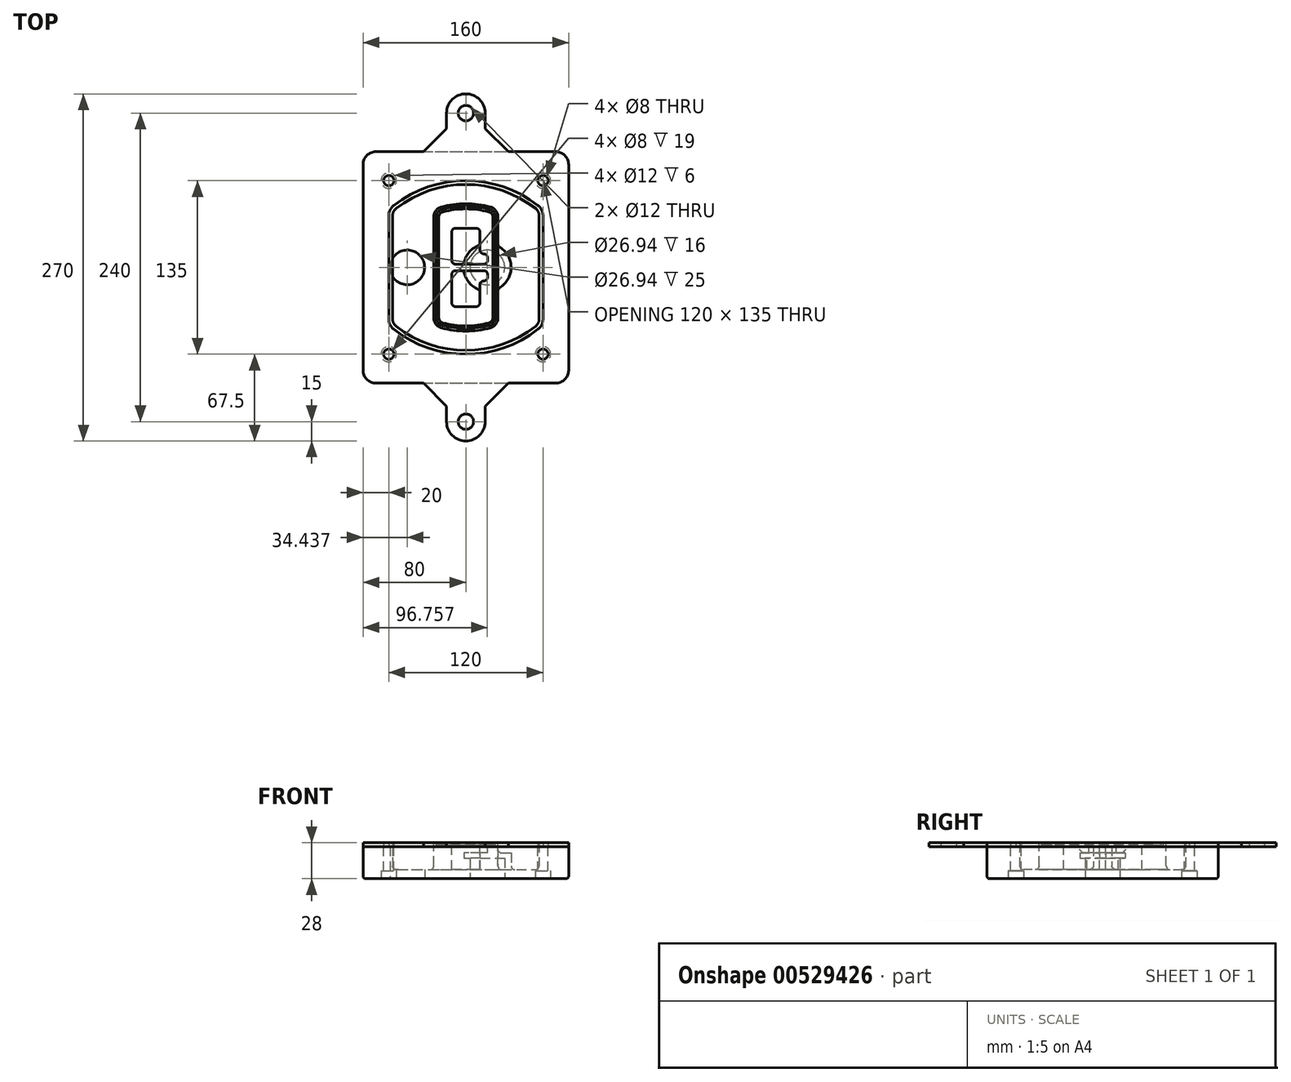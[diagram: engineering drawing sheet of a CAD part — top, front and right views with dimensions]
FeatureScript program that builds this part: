
annotation { "Feature Type Name" : "Feature", "Feature Type Description" : "" }
export const myFeature = defineFeature(function(context is Context, id is Id, definition is map)
    precondition{}
    {
        {
            var Q0;
            Q0=qCreatedBy(makeId("Top.planeOp"),FACE);
            var sketch = newSketch(context, id + "F0", { "sketchPlane" : qUnion([Q0])});
            skPoint(sketch, "E0.rect.middle", {"position": v(0, 0) * mm});
            skLineSegment(sketch, "E1.bottom", {"start": v(-70, -90) * mm, "end": v(70, -90) * mm});
            skLineSegment(sketch, "E1.top", {"start": v(-70, 90) * mm, "end": v(70, 90) * mm});
            skLineSegment(sketch, "E1.left", {"start": v(-80, -80) * mm, "end": v(-80, 80) * mm});
            skLineSegment(sketch, "E1.right", {"start": v(80, -80) * mm, "end": v(80, 80) * mm});
            skLineSegment(sketch, "E2", {"start": v(-80, 90) * mm, "end": v(80, -90) * mm, "construction": true});
            skLineSegment(sketch, "E3", {"start": v(80, 90) * mm, "end": v(-80, -90) * mm, "construction": true});
            skCircle(sketch, "E4", {"center": v(-60, 67.5) * mm, "radius": 4 * mm});
            skCircle(sketch, "E5", {"center": v(60, 67.5) * mm, "radius": 4 * mm});
            skCircle(sketch, "E6", {"center": v(60, -67.5) * mm, "radius": 4 * mm});
            skCircle(sketch, "E7", {"center": v(-60, -67.5) * mm, "radius": 4 * mm});
            skLineSegment(sketch, "E8", {"start": v(-60, 67.5) * mm, "end": v(60, 67.5) * mm, "construction": true});
            skLineSegment(sketch, "E9", {"start": v(60, 67.5) * mm, "end": v(60, -67.5) * mm, "construction": true});
            skLineSegment(sketch, "E10", {"start": v(60, -67.5) * mm, "end": v(-60, -67.5) * mm, "construction": true});
            skLineSegment(sketch, "E11", {"start": v(-60, -67.5) * mm, "end": v(-60, 67.5) * mm, "construction": true});
            skLineSegment(sketch, "E12", {"start": v(-60, 40.3) * mm, "end": v(-60, -40.3) * mm});
            skLineSegment(sketch, "E13", {"start": v(60, 40.3) * mm, "end": v(60, -40.3) * mm});
            skArc(sketch, "E14", {"start": v(56.15, 48.18) * mm, "mid": v(0, 67.5) * mm, "end": v(-56.15, 48.18) * mm});
            skArc(sketch, "E15", {"start": v(-56.15, -48.18) * mm, "mid": v(0, -67.5) * mm, "end": v(56.15, -48.18) * mm});
            skLineSegment(sketch, "E16", {"start": v(-60, 0) * mm, "end": v(60, 0) * mm, "construction": true});
            skPoint(sketch, "E17.visualSharp", {"position": v(-60, -45) * mm});
            skArc(sketch, "E17.filletArc", {"start": v(-60, -40.3) * mm, "mid": v(-58.99, -44.68) * mm, "end": v(-56.15, -48.18) * mm});
            skPoint(sketch, "E18.visualSharp", {"position": v(-60, 45) * mm});
            skArc(sketch, "E18.filletArc", {"start": v(-56.15, 48.18) * mm, "mid": v(-58.99, 44.68) * mm, "end": v(-60, 40.3) * mm});
            skPoint(sketch, "E19.visualSharp", {"position": v(60, 45) * mm});
            skArc(sketch, "E19.filletArc", {"start": v(60, 40.3) * mm, "mid": v(58.99, 44.68) * mm, "end": v(56.15, 48.18) * mm});
            skPoint(sketch, "E20.visualSharp", {"position": v(60, -45) * mm});
            skArc(sketch, "E20.filletArc", {"start": v(56.15, -48.18) * mm, "mid": v(58.99, -44.68) * mm, "end": v(60, -40.3) * mm});
            skPoint(sketch, "E21.visualSharp", {"position": v(-80, 90) * mm});
            skArc(sketch, "E21.filletArc", {"start": v(-70, 90) * mm, "mid": v(-77.07, 87.07) * mm, "end": v(-80, 80) * mm});
            skPoint(sketch, "E22.visualSharp", {"position": v(80, 90) * mm});
            skArc(sketch, "E22.filletArc", {"start": v(80, 80) * mm, "mid": v(77.07, 87.07) * mm, "end": v(70, 90) * mm});
            skPoint(sketch, "E23.visualSharp", {"position": v(80, -90) * mm});
            skArc(sketch, "E23.filletArc", {"start": v(70, -90) * mm, "mid": v(77.07, -87.07) * mm, "end": v(80, -80) * mm});
            skPoint(sketch, "E24.visualSharp", {"position": v(-80, -90) * mm});
            skArc(sketch, "E24.filletArc", {"start": v(-80, -80) * mm, "mid": v(-77.07, -87.07) * mm, "end": v(-70, -90) * mm});
            skArc(sketch, "E25.0", {"start": v(57, 40.3) * mm, "mid": v(56.3, 43.36) * mm, "end": v(54.3, 45.81) * mm});
            skLineSegment(sketch, "E25.1", {"start": v(57, 40.3) * mm, "end": v(57, -40.3) * mm});
            skArc(sketch, "E25.2", {"start": v(54.3, -45.81) * mm, "mid": v(56.3, -43.36) * mm, "end": v(57, -40.3) * mm});
            skArc(sketch, "E25.3", {"start": v(-54.3, -45.81) * mm, "mid": v(0, -64.5) * mm, "end": v(54.3, -45.81) * mm});
            skArc(sketch, "E25.4", {"start": v(-57, -40.3) * mm, "mid": v(-56.3, -43.36) * mm, "end": v(-54.3, -45.81) * mm});
            skArc(sketch, "E25.5", {"start": v(54.3, 45.81) * mm, "mid": v(0, 64.5) * mm, "end": v(-54.3, 45.81) * mm});
            skLineSegment(sketch, "E25.6", {"start": v(-57, 40.3) * mm, "end": v(-57, -40.3) * mm});
            skArc(sketch, "E25.7", {"start": v(-54.3, 45.81) * mm, "mid": v(-56.3, 43.36) * mm, "end": v(-57, 40.3) * mm});
            skArc(sketch, "E26.0", {"start": v(-58.62, 51.33) * mm, "mid": v(-62.58, 46.43) * mm, "end": v(-64, 40.3) * mm});
            skArc(sketch, "E26.1", {"start": v(58.62, 51.33) * mm, "mid": v(0, 71.5) * mm, "end": v(-58.62, 51.33) * mm});
            skArc(sketch, "E26.2", {"start": v(64, 40.3) * mm, "mid": v(62.58, 46.43) * mm, "end": v(58.62, 51.33) * mm});
            skLineSegment(sketch, "E26.3", {"start": v(64, 40.3) * mm, "end": v(64, -40.3) * mm});
            skArc(sketch, "E26.4", {"start": v(58.62, -51.33) * mm, "mid": v(62.58, -46.43) * mm, "end": v(64, -40.3) * mm});
            skLineSegment(sketch, "E26.5", {"start": v(-64, 40.3) * mm, "end": v(-64, -40.3) * mm});
            skArc(sketch, "E26.6", {"start": v(-58.62, -51.33) * mm, "mid": v(0, -71.5) * mm, "end": v(58.62, -51.33) * mm});
            skArc(sketch, "E26.7", {"start": v(-64, -40.3) * mm, "mid": v(-62.58, -46.43) * mm, "end": v(-58.62, -51.33) * mm});
            skSolve(sketch);
        }
        {
            var Q0;
            Q0=makeQuery(id+"F0.imprint","IMPRINT",FACE,{"disambiguationData":[TD([[makeQuery(id+"F0.imprint","IMPRINT",EDGE,{"derivedFrom":sQuery(id+"F0.wireOp",EDGE,"E1.bottom")}),1.0]])]});
            var Q1;
            Q1=makeQuery(id+"F0.imprint","IMPRINT",FACE,{"disambiguationData":[TD([[makeQuery(id+"F0.imprint","IMPRINT",EDGE,{"derivedFrom":sQuery(id+"F0.wireOp",EDGE,"E12")}),1.0]])]});
            var Q2;
            Q2=makeQuery(id+"F0.imprint","IMPRINT",FACE,{"disambiguationData":[TD([[makeQuery(id+"F0.imprint","IMPRINT",EDGE,{"derivedFrom":sQuery(id+"F0.wireOp",EDGE,"E25.0")}),1.0]])]});
            var Q3;
            Q3=makeQuery(id+"F0.imprint","IMPRINT",FACE,{"disambiguationData":[TD([[makeQuery(id+"F0.imprint","IMPRINT",EDGE,{"derivedFrom":sQuery(id+"F0.wireOp",EDGE,"E12")}),-1.0]])]});
            extrude(context, id + "F1", {"entities" : qUnion([Q0, Q1, Q2, Q3]), "oppositeDirection" : true, "depth" : 25 * mm});
        }
        {
            var Q0;
            Q0=makeQuery(id+"F0.imprint","IMPRINT",FACE,{"disambiguationData":[TD([[makeQuery(id+"F0.imprint","IMPRINT",EDGE,{"derivedFrom":sQuery(id+"F0.wireOp",EDGE,"E12")}),1.0]])]});
            extrude(context, id + "F2", {"entities" : qUnion([Q0]), "operationType" : NewBodyOperationType.ADD, "depth" : 3 * mm});
        }
        {
            var Q0;
            Q0=makeQuery(id+"F0.imprint","IMPRINT",FACE,{"disambiguationData":[TD([[makeQuery(id+"F0.imprint","IMPRINT",EDGE,{"derivedFrom":sQuery(id+"F0.wireOp",EDGE,"E25.0")}),1.0]])]});
            extrude(context, id + "F3", {"entities" : qUnion([Q0]), "operationType" : NewBodyOperationType.REMOVE, "oppositeDirection" : true, "depth" : 18 * mm});
        }
        {
            var Q0;
            Q0=makeQuery(id+"F2.opExtrude","CAP_FACE",FACE,{"disambiguationData":[OSD([sQuery(id+"F0.wireOp",EDGE,"E12"),sQuery(id+"F0.wireOp",EDGE,"E13"),sQuery(id+"F0.wireOp",EDGE,"E14"),sQuery(id+"F0.wireOp",EDGE,"E15"),sQuery(id+"F0.wireOp",EDGE,"E17.filletArc"),sQuery(id+"F0.wireOp",EDGE,"E18.filletArc"),sQuery(id+"F0.wireOp",EDGE,"E19.filletArc"),sQuery(id+"F0.wireOp",EDGE,"E20.filletArc"),sQuery(id+"F0.wireOp",EDGE,"E25.0"),sQuery(id+"F0.wireOp",EDGE,"E25.1"),sQuery(id+"F0.wireOp",EDGE,"E25.2"),sQuery(id+"F0.wireOp",EDGE,"E25.3"),sQuery(id+"F0.wireOp",EDGE,"E25.4"),sQuery(id+"F0.wireOp",EDGE,"E25.5"),sQuery(id+"F0.wireOp",EDGE,"E25.6"),sQuery(id+"F0.wireOp",EDGE,"E25.7")])],"isStart":false});
            var sketch = newSketch(context, id + "F4", { "sketchPlane" : qUnion([Q0])});
            skArc(sketch, "E27.0", {"start": v(-19.08, -46.97) * mm, "mid": v(0, -49.5) * mm, "end": v(19.08, -46.97) * mm});
            skArc(sketch, "E28.0", {"start": v(19.08, 46.97) * mm, "mid": v(0, 49.5) * mm, "end": v(-19.08, 46.97) * mm});
            skLineSegment(sketch, "E29", {"start": v(-25, 39.25) * mm, "end": v(-25, -39.25) * mm});
            skLineSegment(sketch, "E30", {"start": v(25, 39.25) * mm, "end": v(25, -39.25) * mm});
            skLineSegment(sketch, "E31", {"start": v(-25, 45.1) * mm, "end": v(25, 45.1) * mm, "construction": true});
            skLineSegment(sketch, "E32", {"start": v(-25, -45.1) * mm, "end": v(25, -45.1) * mm, "construction": true});
            skPoint(sketch, "E33.visualSharp", {"position": v(-25, 45.1) * mm});
            skArc(sketch, "E33.filletArc", {"start": v(-19.08, 46.97) * mm, "mid": v(-23.35, 44.11) * mm, "end": v(-25, 39.25) * mm});
            skPoint(sketch, "E34.visualSharp", {"position": v(25, 45.1) * mm});
            skArc(sketch, "E34.filletArc", {"start": v(25, 39.25) * mm, "mid": v(23.35, 44.11) * mm, "end": v(19.08, 46.97) * mm});
            skPoint(sketch, "E35.visualSharp", {"position": v(25, -45.1) * mm});
            skArc(sketch, "E35.filletArc", {"start": v(19.08, -46.97) * mm, "mid": v(23.35, -44.11) * mm, "end": v(25, -39.25) * mm});
            skPoint(sketch, "E36.visualSharp", {"position": v(-25, -45.1) * mm});
            skArc(sketch, "E36.filletArc", {"start": v(-25, -39.25) * mm, "mid": v(-23.35, -44.11) * mm, "end": v(-19.08, -46.97) * mm});
            skArc(sketch, "E37.0", {"start": v(54.3, 45.81) * mm, "mid": v(0, 64.5) * mm, "end": v(-54.3, 45.81) * mm});
            skArc(sketch, "E37.1", {"start": v(-54.3, 45.81) * mm, "mid": v(-56.3, 43.36) * mm, "end": v(-57, 40.3) * mm});
            skLineSegment(sketch, "E37.2", {"start": v(-57, 40.3) * mm, "end": v(-57, -40.3) * mm});
            skArc(sketch, "E37.3", {"start": v(-57, -40.3) * mm, "mid": v(-56.3, -43.36) * mm, "end": v(-54.3, -45.81) * mm});
            skArc(sketch, "E37.4", {"start": v(-54.3, -45.81) * mm, "mid": v(0, -64.5) * mm, "end": v(54.3, -45.81) * mm});
            skArc(sketch, "E37.5", {"start": v(54.3, -45.81) * mm, "mid": v(56.3, -43.36) * mm, "end": v(57, -40.3) * mm});
            skLineSegment(sketch, "E37.6", {"start": v(57, 40.3) * mm, "end": v(57, -40.3) * mm});
            skArc(sketch, "E37.7", {"start": v(57, 40.3) * mm, "mid": v(56.3, 43.36) * mm, "end": v(54.3, 45.81) * mm});
            skLineSegment(sketch, "E38.0", {"start": v(23, 39.25) * mm, "end": v(23, -39.25) * mm});
            skArc(sketch, "E38.1", {"start": v(18.56, -45.04) * mm, "mid": v(21.76, -42.9) * mm, "end": v(23, -39.25) * mm});
            skArc(sketch, "E38.2", {"start": v(-18.56, -45.04) * mm, "mid": v(0, -47.5) * mm, "end": v(18.56, -45.04) * mm});
            skArc(sketch, "E38.3", {"start": v(-23, -39.25) * mm, "mid": v(-21.76, -42.9) * mm, "end": v(-18.56, -45.04) * mm});
            skLineSegment(sketch, "E38.4", {"start": v(-23, 39.25) * mm, "end": v(-23, -39.25) * mm});
            skArc(sketch, "E38.5", {"start": v(23, 39.25) * mm, "mid": v(21.76, 42.9) * mm, "end": v(18.56, 45.04) * mm});
            skArc(sketch, "E38.6", {"start": v(-18.56, 45.04) * mm, "mid": v(-21.76, 42.9) * mm, "end": v(-23, 39.25) * mm});
            skArc(sketch, "E38.7", {"start": v(18.56, 45.04) * mm, "mid": v(0, 47.5) * mm, "end": v(-18.56, 45.04) * mm});
            skArc(sketch, "E39.0", {"start": v(21, 39.25) * mm, "mid": v(20.18, 41.68) * mm, "end": v(18.04, 43.1) * mm});
            skLineSegment(sketch, "E39.1", {"start": v(21, 39.25) * mm, "end": v(21, -39.25) * mm});
            skArc(sketch, "E39.2", {"start": v(18.04, -43.1) * mm, "mid": v(20.18, -41.68) * mm, "end": v(21, -39.25) * mm});
            skArc(sketch, "E39.3", {"start": v(-18.04, -43.1) * mm, "mid": v(0, -45.5) * mm, "end": v(18.04, -43.1) * mm});
            skArc(sketch, "E39.4", {"start": v(-21, -39.25) * mm, "mid": v(-20.18, -41.68) * mm, "end": v(-18.04, -43.1) * mm});
            skArc(sketch, "E39.5", {"start": v(18.04, 43.1) * mm, "mid": v(0, 45.5) * mm, "end": v(-18.04, 43.1) * mm});
            skLineSegment(sketch, "E39.6", {"start": v(-21, 39.25) * mm, "end": v(-21, -39.25) * mm});
            skArc(sketch, "E39.7", {"start": v(-18.04, 43.1) * mm, "mid": v(-20.18, 41.68) * mm, "end": v(-21, 39.25) * mm});
            skLineSegment(sketch, "E40", {"start": v(-25, 0) * mm, "end": v(25, 0) * mm, "construction": true});
            skLineSegment(sketch, "E41", {"start": v(-11, 5.5) * mm, "end": v(-11, 27.5) * mm});
            skLineSegment(sketch, "E42", {"start": v(-8, 30.5) * mm, "end": v(8, 30.5) * mm});
            skLineSegment(sketch, "E43", {"start": v(11, 27.5) * mm, "end": v(11, 13.5) * mm});
            skLineSegment(sketch, "E44", {"start": v(14, 10.5) * mm, "end": v(14, 10.5) * mm});
            skLineSegment(sketch, "E45", {"start": v(17, 7.5) * mm, "end": v(17, 5.5) * mm});
            skLineSegment(sketch, "E46", {"start": v(14, 2.5) * mm, "end": v(-8, 2.5) * mm});
            skPoint(sketch, "E47.visualSharp", {"position": v(-11, 30.5) * mm});
            skArc(sketch, "E47.filletArc", {"start": v(-8, 30.5) * mm, "mid": v(-10.12, 29.62) * mm, "end": v(-11, 27.5) * mm});
            skPoint(sketch, "E48.visualSharp", {"position": v(11, 30.5) * mm});
            skArc(sketch, "E48.filletArc", {"start": v(11, 27.5) * mm, "mid": v(10.12, 29.62) * mm, "end": v(8, 30.5) * mm});
            skPoint(sketch, "E49.visualSharp", {"position": v(11, 10.5) * mm});
            skArc(sketch, "E49.filletArc", {"start": v(11, 13.5) * mm, "mid": v(11.88, 11.38) * mm, "end": v(14, 10.5) * mm});
            skPoint(sketch, "E50.visualSharp", {"position": v(17, 10.5) * mm});
            skArc(sketch, "E50.filletArc", {"start": v(17, 7.5) * mm, "mid": v(16.12, 9.62) * mm, "end": v(14, 10.5) * mm});
            skPoint(sketch, "E51.visualSharp", {"position": v(17, 2.5) * mm});
            skArc(sketch, "E51.filletArc", {"start": v(14, 2.5) * mm, "mid": v(16.12, 3.38) * mm, "end": v(17, 5.5) * mm});
            skPoint(sketch, "E52.visualSharp", {"position": v(-11, 2.5) * mm});
            skArc(sketch, "E52.filletArc", {"start": v(-11, 5.5) * mm, "mid": v(-10.12, 3.38) * mm, "end": v(-8, 2.5) * mm});
            skLineSegment(sketch, "E53.0.MirrorCS", {"start": v(14, -2.5) * mm, "end": v(-8, -2.5) * mm});
            skArc(sketch, "E54.0.MirrorCS", {"start": v(-11, -5.5) * mm, "mid": v(-10.12, -3.38) * mm, "end": v(-8, -2.5) * mm});
            skLineSegment(sketch, "E55.0.MirrorCS", {"start": v(-11, -5.5) * mm, "end": v(-11, -27.5) * mm});
            skArc(sketch, "E56.0.MirrorCS", {"start": v(-8, -30.5) * mm, "mid": v(-10.12, -29.62) * mm, "end": v(-11, -27.5) * mm});
            skLineSegment(sketch, "E57.0.MirrorCS", {"start": v(-8, -30.5) * mm, "end": v(8, -30.5) * mm});
            skArc(sketch, "E58.0.MirrorCS", {"start": v(11, -27.5) * mm, "mid": v(10.12, -29.62) * mm, "end": v(8, -30.5) * mm});
            skLineSegment(sketch, "E59.0.MirrorCS", {"start": v(11, -27.5) * mm, "end": v(11, -13.5) * mm});
            skArc(sketch, "E60.0.MirrorCS", {"start": v(11, -13.5) * mm, "mid": v(11.88, -11.38) * mm, "end": v(14, -10.5) * mm});
            skArc(sketch, "E61.0.MirrorCS", {"start": v(17, -7.5) * mm, "mid": v(16.12, -9.62) * mm, "end": v(14, -10.5) * mm});
            skLineSegment(sketch, "E62.0.MirrorCS", {"start": v(17, -7.5) * mm, "end": v(17, -5.5) * mm});
            skArc(sketch, "E63.0.MirrorCS", {"start": v(14, -2.5) * mm, "mid": v(16.12, -3.38) * mm, "end": v(17, -5.5) * mm});
            skSolve(sketch);
        }
        {
            var Q0;
            Q0=makeQuery(id+"F4.imprint","IMPRINT",FACE,{"disambiguationData":[TD([[makeQuery(id+"F4.imprint","IMPRINT",EDGE,{"derivedFrom":sQuery(id+"F4.wireOp",EDGE,"E27.0")}),1.0]])]});
            var Q1;
            Q1=makeQuery(id+"F4.imprint","IMPRINT",FACE,{"disambiguationData":[TD([[makeQuery(id+"F4.imprint","IMPRINT",EDGE,{"derivedFrom":sQuery(id+"F4.wireOp",EDGE,"E38.0")}),-1.0]])]});
            var Q2;
            Q2=makeQuery(id+"F4.imprint","IMPRINT",FACE,{"disambiguationData":[TD([[makeQuery(id+"F4.imprint","IMPRINT",EDGE,{"derivedFrom":sQuery(id+"F4.wireOp",EDGE,"E39.0")}),1.0]])]});
            extrude(context, id + "F5", {"entities" : qUnion([Q0, Q1, Q2]), "operationType" : NewBodyOperationType.ADD, "endBound" : BoundingType.UP_TO_NEXT, "oppositeDirection" : true, "depth" : 25 * mm});
        }
        {
            var Q0;
            Q0=makeQuery(id+"F4.imprint","IMPRINT",FACE,{"disambiguationData":[TD([[makeQuery(id+"F4.imprint","IMPRINT",EDGE,{"derivedFrom":sQuery(id+"F4.wireOp",EDGE,"E38.0")}),-1.0]])]});
            extrude(context, id + "F6", {"entities" : qUnion([Q0]), "operationType" : NewBodyOperationType.REMOVE, "oppositeDirection" : true, "depth" : 2 * mm, "offsetDistance" : 25 * mm});
        }
        {
            var Q0;
            Q0=makeQuery(id+"F1.opExtrude","CAP_FACE",FACE,{"disambiguationData":[OSD([sQuery(id+"F0.wireOp",EDGE,"E1.bottom"),sQuery(id+"F0.wireOp",EDGE,"E1.top"),sQuery(id+"F0.wireOp",EDGE,"E1.left"),sQuery(id+"F0.wireOp",EDGE,"E1.right"),sQuery(id+"F0.wireOp",EDGE,"E4"),sQuery(id+"F0.wireOp",EDGE,"E5"),sQuery(id+"F0.wireOp",EDGE,"E6"),sQuery(id+"F0.wireOp",EDGE,"E7"),sQuery(id+"F0.wireOp",EDGE,"E21.filletArc"),sQuery(id+"F0.wireOp",EDGE,"E22.filletArc"),sQuery(id+"F0.wireOp",EDGE,"E23.filletArc"),sQuery(id+"F0.wireOp",EDGE,"E24.filletArc")])],"isStart":false});
            var sketch = newSketch(context, id + "F7", { "sketchPlane" : qUnion([Q0])});
            skCircle(sketch, "E64", {"center": v(16.76, 0) * mm, "radius": 13.47 * mm});
            skCircle(sketch, "E65", {"center": v(-45.56, 0) * mm, "radius": 13.47 * mm});
            skLineSegment(sketch, "E66", {"start": v(80, 0) * mm, "end": v(-80, 0) * mm});
            skCircle(sketch, "E67", {"center": v(16.76, 0) * mm, "radius": 18.47 * mm});
            skCircle(sketch, "E68", {"center": v(60, -67.5) * mm, "radius": 6 * mm});
            skCircle(sketch, "E69", {"center": v(-60, -67.5) * mm, "radius": 6 * mm});
            skCircle(sketch, "E70", {"center": v(-60, 67.5) * mm, "radius": 6 * mm});
            skCircle(sketch, "E71", {"center": v(60, 67.5) * mm, "radius": 6 * mm});
            skSolve(sketch);
        }
        {
            var Q0;
            {var subQ1=sQuery(id+"F7.wireOp",EDGE,"E66");var subQ4=sQuery(id+"F7.wireOp",EDGE,"E64");var subQ6=makeQuery(id+"F7.imprint","INTERSECT",VERTEX,{"disambiguationData":[OD(0.0)],"derivedFrom":[subQ4,subQ1]});Q0=makeQuery(id+"F7.imprint","IMPRINT",FACE,{"disambiguationData":[TD([[makeQuery(id+"F7.imprint","IMPRINT",EDGE,{"disambiguationData":[TD([[subQ6,-1.0]])],"derivedFrom":subQ4}),-1.0]])]});}
            var Q1;
            {var subQ0=sQuery(id+"F7.wireOp",EDGE,"E66");var subQ1=sQuery(id+"F7.wireOp",EDGE,"E64");var subQ3=makeQuery(id+"F7.imprint","INTERSECT",VERTEX,{"disambiguationData":[OD(0.0)],"derivedFrom":[subQ1,subQ0]});Q1=makeQuery(id+"F7.imprint","IMPRINT",FACE,{"disambiguationData":[TD([[makeQuery(id+"F7.imprint","IMPRINT",EDGE,{"disambiguationData":[TD([[subQ3,-1.0]])],"derivedFrom":subQ1}),1.0]])]});}
            var Q2;
            {var subQ0=sQuery(id+"F7.wireOp",EDGE,"E66");var subQ1=sQuery(id+"F7.wireOp",EDGE,"E64");var subQ3=makeQuery(id+"F7.imprint","INTERSECT",VERTEX,{"disambiguationData":[OD(0.0)],"derivedFrom":[subQ1,subQ0]});Q2=makeQuery(id+"F7.imprint","IMPRINT",FACE,{"disambiguationData":[TD([[makeQuery(id+"F7.imprint","IMPRINT",EDGE,{"disambiguationData":[TD([[subQ3,1.0]])],"derivedFrom":subQ1}),1.0]])]});}
            var Q3;
            {var subQ1=sQuery(id+"F7.wireOp",EDGE,"E66");var subQ4=sQuery(id+"F7.wireOp",EDGE,"E64");var subQ6=makeQuery(id+"F7.imprint","INTERSECT",VERTEX,{"disambiguationData":[OD(0.0)],"derivedFrom":[subQ4,subQ1]});Q3=makeQuery(id+"F7.imprint","IMPRINT",FACE,{"disambiguationData":[TD([[makeQuery(id+"F7.imprint","IMPRINT",EDGE,{"disambiguationData":[TD([[subQ6,1.0]])],"derivedFrom":subQ4}),-1.0]])]});}
            extrude(context, id + "F8", {"entities" : qUnion([Q0, Q1, Q2, Q3]), "operationType" : NewBodyOperationType.ADD, "oppositeDirection" : true, "depth" : 20 * mm});
        }
        {
            var Q0;
            {var subQ0=sQuery(id+"F7.wireOp",EDGE,"E66");var subQ1=sQuery(id+"F7.wireOp",EDGE,"E64");var subQ3=makeQuery(id+"F7.imprint","INTERSECT",VERTEX,{"disambiguationData":[OD(0.0)],"derivedFrom":[subQ1,subQ0]});Q0=makeQuery(id+"F7.imprint","IMPRINT",FACE,{"disambiguationData":[TD([[makeQuery(id+"F7.imprint","IMPRINT",EDGE,{"disambiguationData":[TD([[subQ3,-1.0]])],"derivedFrom":subQ1}),1.0]])]});}
            var Q1;
            {var subQ0=sQuery(id+"F7.wireOp",EDGE,"E66");var subQ1=sQuery(id+"F7.wireOp",EDGE,"E64");var subQ3=makeQuery(id+"F7.imprint","INTERSECT",VERTEX,{"disambiguationData":[OD(0.0)],"derivedFrom":[subQ1,subQ0]});Q1=makeQuery(id+"F7.imprint","IMPRINT",FACE,{"disambiguationData":[TD([[makeQuery(id+"F7.imprint","IMPRINT",EDGE,{"disambiguationData":[TD([[subQ3,1.0]])],"derivedFrom":subQ1}),1.0]])]});}
            extrude(context, id + "F9", {"entities" : qUnion([Q0, Q1]), "operationType" : NewBodyOperationType.REMOVE, "oppositeDirection" : true, "depth" : 16 * mm});
        }
        {
            var Q0;
            {var subQ0=sQuery(id+"F7.wireOp",EDGE,"E66");var subQ1=sQuery(id+"F7.wireOp",EDGE,"E65");var subQ3=makeQuery(id+"F7.imprint","INTERSECT",VERTEX,{"disambiguationData":[OD(0.0)],"derivedFrom":[subQ1,subQ0]});Q0=makeQuery(id+"F7.imprint","IMPRINT",FACE,{"disambiguationData":[TD([[makeQuery(id+"F7.imprint","IMPRINT",EDGE,{"disambiguationData":[TD([[subQ3,-1.0]])],"derivedFrom":subQ1}),1.0]])]});}
            var Q1;
            {var subQ0=sQuery(id+"F7.wireOp",EDGE,"E66");var subQ1=sQuery(id+"F7.wireOp",EDGE,"E65");var subQ3=makeQuery(id+"F7.imprint","INTERSECT",VERTEX,{"disambiguationData":[OD(0.0)],"derivedFrom":[subQ1,subQ0]});Q1=makeQuery(id+"F7.imprint","IMPRINT",FACE,{"disambiguationData":[TD([[makeQuery(id+"F7.imprint","IMPRINT",EDGE,{"disambiguationData":[TD([[subQ3,1.0]])],"derivedFrom":subQ1}),1.0]])]});}
            extrude(context, id + "F10", {"entities" : qUnion([Q0, Q1]), "operationType" : NewBodyOperationType.REMOVE, "oppositeDirection" : true, "depth" : 25 * mm});
        }
        {
            var Q0;
            Q0=makeQuery(id+"F7.imprint","IMPRINT",FACE,{"disambiguationData":[TD([[makeQuery(id+"F7.imprint","IMPRINT",EDGE,{"derivedFrom":sQuery(id+"F7.wireOp",EDGE,"E68")}),1.0]])]});
            var Q1;
            Q1=makeQuery(id+"F7.imprint","IMPRINT",FACE,{"disambiguationData":[TD([[makeQuery(id+"F7.imprint","IMPRINT",EDGE,{"derivedFrom":makeQuery(id+"F1.opExtrude","CAP_EDGE",EDGE,{"disambiguationData":[OSD([sQuery(id+"F0.wireOp",EDGE,"E5")])],"isStart":false})}),-1.0]])]});
            var Q2;
            Q2=makeQuery(id+"F7.imprint","IMPRINT",FACE,{"disambiguationData":[TD([[makeQuery(id+"F7.imprint","IMPRINT",EDGE,{"derivedFrom":sQuery(id+"F7.wireOp",EDGE,"E69")}),1.0]])]});
            var Q3;
            Q3=makeQuery(id+"F7.imprint","IMPRINT",FACE,{"disambiguationData":[TD([[makeQuery(id+"F7.imprint","IMPRINT",EDGE,{"derivedFrom":makeQuery(id+"F1.opExtrude","CAP_EDGE",EDGE,{"disambiguationData":[OSD([sQuery(id+"F0.wireOp",EDGE,"E4")])],"isStart":false})}),-1.0]])]});
            var Q4;
            Q4=makeQuery(id+"F7.imprint","IMPRINT",FACE,{"disambiguationData":[TD([[makeQuery(id+"F7.imprint","IMPRINT",EDGE,{"derivedFrom":sQuery(id+"F7.wireOp",EDGE,"E70")}),1.0]])]});
            var Q5;
            Q5=makeQuery(id+"F7.imprint","IMPRINT",FACE,{"disambiguationData":[TD([[makeQuery(id+"F7.imprint","IMPRINT",EDGE,{"derivedFrom":makeQuery(id+"F1.opExtrude","CAP_EDGE",EDGE,{"disambiguationData":[OSD([sQuery(id+"F0.wireOp",EDGE,"E7")])],"isStart":false})}),-1.0]])]});
            var Q6;
            Q6=makeQuery(id+"F7.imprint","IMPRINT",FACE,{"disambiguationData":[TD([[makeQuery(id+"F7.imprint","IMPRINT",EDGE,{"derivedFrom":sQuery(id+"F7.wireOp",EDGE,"E71")}),1.0]])]});
            var Q7;
            Q7=makeQuery(id+"F7.imprint","IMPRINT",FACE,{"disambiguationData":[TD([[makeQuery(id+"F7.imprint","IMPRINT",EDGE,{"derivedFrom":makeQuery(id+"F1.opExtrude","CAP_EDGE",EDGE,{"disambiguationData":[OSD([sQuery(id+"F0.wireOp",EDGE,"E6")])],"isStart":false})}),-1.0]])]});
            extrude(context, id + "F11", {"entities" : qUnion([Q0, Q1, Q2, Q3, Q4, Q5, Q6, Q7]), "operationType" : NewBodyOperationType.REMOVE, "oppositeDirection" : true, "depth" : 6 * mm});
        }
        {
            var Q0;
            Q0=makeQuery(id+"F9.boolean.opBoolean","COPY",FACE,{"derivedFrom":makeQuery(id+"F9.opExtrude","CAP_FACE",FACE,{"disambiguationData":[OSD([sQuery(id+"F7.wireOp",EDGE,"E64")])],"isStart":false})});
            var sketch = newSketch(context, id + "F12", { "sketchPlane" : qUnion([Q0])});
            skArc(sketch, "E72.0", {"start": v(11, 17.55) * mm, "mid": v(2.57, 11.82) * mm, "end": v(-1.54, 2.5) * mm});
            skArc(sketch, "E72.1", {"start": v(-1.54, -2.5) * mm, "mid": v(2.57, -11.82) * mm, "end": v(11, -17.55) * mm});
            skLineSegment(sketch, "E73", {"start": v(-1.54, -2.5) * mm, "end": v(14, -2.5) * mm});
            skLineSegment(sketch, "E74.0", {"start": v(14, 2.5) * mm, "end": v(-1.54, 2.5) * mm});
            skArc(sketch, "E74.1", {"start": v(14, 2.5) * mm, "mid": v(16.12, 3.38) * mm, "end": v(17, 5.5) * mm});
            skLineSegment(sketch, "E74.2", {"start": v(17, 7.5) * mm, "end": v(17, 5.5) * mm});
            skArc(sketch, "E74.3", {"start": v(17, 7.5) * mm, "mid": v(16.12, 9.62) * mm, "end": v(14, 10.5) * mm});
            skArc(sketch, "E74.4", {"start": v(11, 13.5) * mm, "mid": v(11.88, 11.38) * mm, "end": v(14, 10.5) * mm});
            skLineSegment(sketch, "E74.5", {"start": v(11, 17.55) * mm, "end": v(11, 13.5) * mm});
            skLineSegment(sketch, "E74.7", {"start": v(14, -2.5) * mm, "end": v(-1.54, -2.5) * mm});
            skArc(sketch, "E74.8", {"start": v(14, -2.5) * mm, "mid": v(16.12, -3.38) * mm, "end": v(17, -5.5) * mm});
            skLineSegment(sketch, "E74.9", {"start": v(17, -7.5) * mm, "end": v(17, -5.5) * mm});
            skArc(sketch, "E74.10", {"start": v(17, -7.5) * mm, "mid": v(16.12, -9.62) * mm, "end": v(14, -10.5) * mm});
            skArc(sketch, "E74.11", {"start": v(11, -13.5) * mm, "mid": v(11.88, -11.38) * mm, "end": v(14, -10.5) * mm});
            skLineSegment(sketch, "E74.12", {"start": v(11, -17.55) * mm, "end": v(11, -13.5) * mm});
            skPoint(sketch, "E75.orphan", {"position": v(11, -27.5) * mm});
            skPoint(sketch, "E76.orphan", {"position": v(-8, -2.5) * mm});
            skPoint(sketch, "E77.orphan", {"position": v(-8, 2.5) * mm});
            skPoint(sketch, "E78.orphan", {"position": v(11, 27.5) * mm});
            skSolve(sketch);
        }
        {
            var Q0;
            {var subQ7=sQuery(id+"F12.wireOp",EDGE,"E72.0");var subQ14=sQuery(id+"F12.wireOp",EDGE,"E72.1");var subQ16=sQuery(id+"F12.wireOp",EDGE,"E74.1");var subQ18=sQuery(id+"F12.wireOp",EDGE,"E74.8");Q0=qUnion([makeQuery(id+"F12.imprint","IMPRINT",FACE,{"disambiguationData":[TD([[makeQuery(id+"F12.imprint","IMPRINT",EDGE,{"derivedFrom":subQ7}),1.0]])]}),makeQuery(id+"F12.imprint","IMPRINT",FACE,{"disambiguationData":[TD([[makeQuery(id+"F12.imprint","IMPRINT",EDGE,{"derivedFrom":subQ14}),1.0]])]}),makeQuery(id+"F12.imprint","IMPRINT",FACE,{"disambiguationData":[TD([[makeQuery(id+"F12.imprint","IMPRINT",EDGE,{"derivedFrom":subQ16}),1.0]])]}),makeQuery(id+"F12.imprint","IMPRINT",FACE,{"disambiguationData":[TD([[makeQuery(id+"F12.imprint","IMPRINT",EDGE,{"derivedFrom":subQ18}),-1.0]])]})]);}
            var Q1;
            Q1=makeQuery(id+"F5.boolean.opBoolean","SPLIT",FACE,{"disambiguationData":[TD([makeQuery(id+"F5.opExtrude","SWEPT_FACE",FACE,{"disambiguationData":[OSD([sQuery(id+"F4.wireOp",EDGE,"E41")])]})])],"derivedFrom":makeQuery(id+"F3.boolean.opBoolean","COPY",FACE,{"derivedFrom":makeQuery(id+"F3.opExtrude","CAP_FACE",FACE,{"disambiguationData":[OSD([sQuery(id+"F0.wireOp",EDGE,"E25.0"),sQuery(id+"F0.wireOp",EDGE,"E25.1"),sQuery(id+"F0.wireOp",EDGE,"E25.2"),sQuery(id+"F0.wireOp",EDGE,"E25.3"),sQuery(id+"F0.wireOp",EDGE,"E25.4"),sQuery(id+"F0.wireOp",EDGE,"E25.5"),sQuery(id+"F0.wireOp",EDGE,"E25.6"),sQuery(id+"F0.wireOp",EDGE,"E25.7")])],"isStart":false})})});
            extrude(context, id + "F13", {"entities" : qUnion([Q0]), "operationType" : NewBodyOperationType.REMOVE, "endBound" : BoundingType.UP_TO_SURFACE, "endBoundEntityFace" : qUnion([Q1]), "depth" : 25 * mm});
        }
        {
            var Q0;
            Q0=makeQuery(id+"F3.boolean.opBoolean","COPY",EDGE,{"derivedFrom":makeQuery(id+"F3.opExtrude","CAP_EDGE",EDGE,{"disambiguationData":[OSD([sQuery(id+"F0.wireOp",EDGE,"E25.6")])],"isStart":false})});
            var Q1;
            Q1=makeQuery(id+"F8.boolean.opBoolean","INTERSECT",EDGE,{"derivedFrom":[makeQuery(id+"F5.opExtrude","SWEPT_FACE",FACE,{"disambiguationData":[OSD([sQuery(id+"F4.wireOp",EDGE,"E30")])]}),makeQuery(id+"F8.opExtrude","CAP_FACE",FACE,{"disambiguationData":[OSD([sQuery(id+"F7.wireOp",EDGE,"E67")])],"isStart":false})]});
            var Q2;
            Q2=makeQuery(id+"F8.boolean.opBoolean","INTERSECT",EDGE,{"disambiguationData":[OD(1.0)],"derivedFrom":[makeQuery(id+"F5.opExtrude","SWEPT_FACE",FACE,{"disambiguationData":[OSD([sQuery(id+"F4.wireOp",EDGE,"E30")])]}),makeQuery(id+"F8.opExtrude","SWEPT_FACE",FACE,{"disambiguationData":[OSD([sQuery(id+"F7.wireOp",EDGE,"E67")])]})]});
            var Q3;
            {var subQ0=sQuery(id+"F4.wireOp",EDGE,"E30");Q3=makeQuery(id+"F8.boolean.opBoolean","SPLIT",EDGE,{"disambiguationData":[TD([makeQuery(id+"F5.opExtrude","SWEPT_FACE",FACE,{"disambiguationData":[OSD([sQuery(id+"F4.wireOp",EDGE,"E35.filletArc")])]})])],"derivedFrom":makeQuery(id+"F5.opExtrude","CAP_EDGE",EDGE,{"disambiguationData":[OSD([subQ0])],"isStart":false})});}
            var Q4;
            {var subQ0=sQuery(id+"F0.wireOp",EDGE,"E25.7");var subQ1=sQuery(id+"F0.wireOp",EDGE,"E25.1");var subQ2=sQuery(id+"F0.wireOp",EDGE,"E25.6");var subQ3=sQuery(id+"F0.wireOp",EDGE,"E25.5");var subQ4=sQuery(id+"F0.wireOp",EDGE,"E25.4");var subQ5=sQuery(id+"F0.wireOp",EDGE,"E25.0");var subQ6=sQuery(id+"F0.wireOp",EDGE,"E25.2");var subQ7=sQuery(id+"F0.wireOp",EDGE,"E25.3");Q4=makeQuery(id+"F8.boolean.opBoolean","INTERSECT",EDGE,{"derivedFrom":[makeQuery(id+"F5.boolean.opBoolean","SPLIT",FACE,{"disambiguationData":[TD([makeQuery(id+"F2.opExtrude","SWEPT_FACE",FACE,{"disambiguationData":[OSD([subQ5])]})])],"derivedFrom":makeQuery(id+"F3.boolean.opBoolean","COPY",FACE,{"derivedFrom":makeQuery(id+"F3.opExtrude","CAP_FACE",FACE,{"disambiguationData":[OSD([subQ5,subQ1,subQ6,subQ7,subQ4,subQ3,subQ2,subQ0])],"isStart":false})})}),makeQuery(id+"F8.opExtrude","SWEPT_FACE",FACE,{"disambiguationData":[OSD([sQuery(id+"F7.wireOp",EDGE,"E67")])]})]});}
            var Q5;
            Q5=makeQuery(id+"F8.boolean.opBoolean","INTERSECT",EDGE,{"disambiguationData":[OD(0.0)],"derivedFrom":[makeQuery(id+"F5.opExtrude","SWEPT_FACE",FACE,{"disambiguationData":[OSD([sQuery(id+"F4.wireOp",EDGE,"E30")])]}),makeQuery(id+"F8.opExtrude","SWEPT_FACE",FACE,{"disambiguationData":[OSD([sQuery(id+"F7.wireOp",EDGE,"E67")])]})]});
            fillet(context, id + "F14", {"entities" : qUnion([Q0, Q1, Q2, Q3, Q4, Q5]), "radius" : 3 * mm, "tangentPropagation" : true, "allowEdgeOverflow" : false});
        }
        {
            var Q0;
            Q0=makeQuery(id+"F1.opExtrude","CAP_EDGE",EDGE,{"disambiguationData":[OSD([sQuery(id+"F0.wireOp",EDGE,"E1.bottom")])],"isStart":false});
            fillet(context, id + "F15", {"entities" : qUnion([Q0]), "radius" : 2 * mm, "tangentPropagation" : true, "allowEdgeOverflow" : false});
        }
        {
            var Q0;
            {var subQ0=sQuery(id+"F0.wireOp",EDGE,"E21.filletArc");var subQ1=sQuery(id+"F0.wireOp",EDGE,"E7");var subQ2=sQuery(id+"F0.wireOp",EDGE,"E6");var subQ3=sQuery(id+"F0.wireOp",EDGE,"E5");var subQ4=sQuery(id+"F0.wireOp",EDGE,"E4");var subQ5=sQuery(id+"F0.wireOp",EDGE,"E22.filletArc");var subQ6=sQuery(id+"F0.wireOp",EDGE,"E1.bottom");var subQ7=sQuery(id+"F0.wireOp",EDGE,"E1.right");var subQ8=sQuery(id+"F0.wireOp",EDGE,"E1.top");var subQ9=sQuery(id+"F0.wireOp",EDGE,"E1.left");var subQ10=sQuery(id+"F0.wireOp",EDGE,"E23.filletArc");var subQ11=sQuery(id+"F0.wireOp",EDGE,"E24.filletArc");Q0=makeQuery(id+"F2.boolean.opBoolean","SPLIT",FACE,{"disambiguationData":[TD([makeQuery(id+"F1.opExtrude","SWEPT_FACE",FACE,{"disambiguationData":[OSD([subQ6])]})])],"derivedFrom":makeQuery(id+"F1.opExtrude","CAP_FACE",FACE,{"disambiguationData":[OSD([subQ6,subQ8,subQ9,subQ7,subQ4,subQ3,subQ2,subQ1,subQ0,subQ5,subQ10,subQ11])],"isStart":true})});}
            var sketch = newSketch(context, id + "F16", { "sketchPlane" : qUnion([Q0])});
            skLineSegment(sketch, "E79.0", {"start": v(-70, 90) * mm, "end": v(70, 90) * mm});
            skArc(sketch, "E79.1", {"start": v(-70, 90) * mm, "mid": v(-77.07, 87.07) * mm, "end": v(-80, 80) * mm});
            skCircle(sketch, "E79.2", {"center": v(-60, 67.5) * mm, "radius": 4 * mm});
            skLineSegment(sketch, "E79.3", {"start": v(-80, -80) * mm, "end": v(-80, 80) * mm});
            skArc(sketch, "E79.4", {"start": v(80, 80) * mm, "mid": v(77.07, 87.07) * mm, "end": v(70, 90) * mm});
            skCircle(sketch, "E79.5", {"center": v(60, 67.5) * mm, "radius": 4 * mm});
            skLineSegment(sketch, "E79.6", {"start": v(80, -80) * mm, "end": v(80, 80) * mm});
            skArc(sketch, "E79.7", {"start": v(70, -90) * mm, "mid": v(77.07, -87.07) * mm, "end": v(80, -80) * mm});
            skLineSegment(sketch, "E79.8", {"start": v(-70, -90) * mm, "end": v(70, -90) * mm});
            skArc(sketch, "E79.9", {"start": v(-80, -80) * mm, "mid": v(-77.07, -87.07) * mm, "end": v(-70, -90) * mm});
            skCircle(sketch, "E79.10", {"center": v(60, -67.5) * mm, "radius": 4 * mm});
            skCircle(sketch, "E79.11", {"center": v(-60, -67.5) * mm, "radius": 4 * mm});
            skArc(sketch, "E79.12", {"start": v(56.15, 48.18) * mm, "mid": v(0, 67.5) * mm, "end": v(-56.15, 48.18) * mm});
            skLineSegment(sketch, "E79.13", {"start": v(60, 40.3) * mm, "end": v(60, -40.3) * mm});
            skArc(sketch, "E79.14", {"start": v(56.15, -48.18) * mm, "mid": v(58.99, -44.68) * mm, "end": v(60, -40.3) * mm});
            skArc(sketch, "E79.15", {"start": v(-56.15, -48.18) * mm, "mid": v(0, -67.5) * mm, "end": v(56.15, -48.18) * mm});
            skLineSegment(sketch, "E79.16", {"start": v(-60, 40.3) * mm, "end": v(-60, -40.3) * mm});
            skLineSegment(sketch, "E80", {"start": v(-15, 108) * mm, "end": v(-15, 120) * mm});
            skLineSegment(sketch, "E81", {"start": v(15, 108) * mm, "end": v(15, 120) * mm});
            skArc(sketch, "E82", {"start": v(15, 120) * mm, "mid": v(0, 135) * mm, "end": v(-15, 120) * mm});
            skCircle(sketch, "E83", {"center": v(0, 120) * mm, "radius": 6 * mm});
            skLineSegment(sketch, "E84", {"start": v(-15, 108) * mm, "end": v(-33, 90) * mm});
            skLineSegment(sketch, "E85", {"start": v(15, 108) * mm, "end": v(33, 90) * mm});
            skLineSegment(sketch, "E86", {"start": v(0, 90) * mm, "end": v(0, 104.25) * mm, "construction": true});
            skLineSegment(sketch, "E87", {"start": v(-80, 0) * mm, "end": v(80, 0) * mm, "construction": true});
            skLineSegment(sketch, "E88.MirrorCS", {"start": v(-15, -108) * mm, "end": v(-15, -120) * mm});
            skCircle(sketch, "E89.MirrorC", {"center": v(0, -120) * mm, "radius": 6 * mm});
            skLineSegment(sketch, "E90.MirrorCS", {"start": v(15, -108) * mm, "end": v(15, -120) * mm});
            skArc(sketch, "E91.MirrorCS", {"start": v(15, -120) * mm, "mid": v(0, -135) * mm, "end": v(-15, -120) * mm});
            skLineSegment(sketch, "E92.MirrorCS", {"start": v(15, -108) * mm, "end": v(33, -90) * mm});
            skLineSegment(sketch, "E93.MirrorCS", {"start": v(-15, -108) * mm, "end": v(-33, -90) * mm});
            skLineSegment(sketch, "E94.MirrorCS", {"start": v(0, -90) * mm, "end": v(0, -104.25) * mm, "construction": true});
            skSolve(sketch);
        }
        {
            var Q0;
            Q0=makeQuery(id+"F16.imprint","IMPRINT",FACE,{"disambiguationData":[TD([[makeQuery(id+"F16.imprint","IMPRINT",EDGE,{"derivedFrom":sQuery(id+"F16.wireOp",EDGE,"E80")}),-1.0]])]});
            var Q1;
            Q1=makeQuery(id+"F16.imprint","IMPRINT",FACE,{"disambiguationData":[TD([[makeQuery(id+"F16.imprint","IMPRINT",EDGE,{"derivedFrom":sQuery(id+"F16.wireOp",EDGE,"E90.MirrorCS")}),-1.0]])]});
            var Q2;
            {var subQ3=sQuery(id+"F16.wireOp",EDGE,"E79.1");Q2=makeQuery(id+"F16.imprint","IMPRINT",FACE,{"disambiguationData":[TD([[makeQuery(id+"F16.imprint","IMPRINT",EDGE,{"derivedFrom":subQ3}),1.0]])]});}
            var Q3;
            Q3=makeQuery(id+"F2.opExtrude","CAP_FACE",FACE,{"disambiguationData":[OSD([sQuery(id+"F0.wireOp",EDGE,"E12"),sQuery(id+"F0.wireOp",EDGE,"E13"),sQuery(id+"F0.wireOp",EDGE,"E14"),sQuery(id+"F0.wireOp",EDGE,"E15"),sQuery(id+"F0.wireOp",EDGE,"E17.filletArc"),sQuery(id+"F0.wireOp",EDGE,"E18.filletArc"),sQuery(id+"F0.wireOp",EDGE,"E19.filletArc"),sQuery(id+"F0.wireOp",EDGE,"E20.filletArc"),sQuery(id+"F0.wireOp",EDGE,"E25.0"),sQuery(id+"F0.wireOp",EDGE,"E25.1"),sQuery(id+"F0.wireOp",EDGE,"E25.2"),sQuery(id+"F0.wireOp",EDGE,"E25.3"),sQuery(id+"F0.wireOp",EDGE,"E25.4"),sQuery(id+"F0.wireOp",EDGE,"E25.5"),sQuery(id+"F0.wireOp",EDGE,"E25.6"),sQuery(id+"F0.wireOp",EDGE,"E25.7")])],"isStart":false});
            extrude(context, id + "F17", {"entities" : qUnion([Q0, Q1, Q2]), "endBound" : BoundingType.UP_TO_SURFACE, "depth" : 25 * mm, "endBoundEntityFace" : qUnion([Q3]), "offsetDistance" : 25 * mm});
        }
    });
